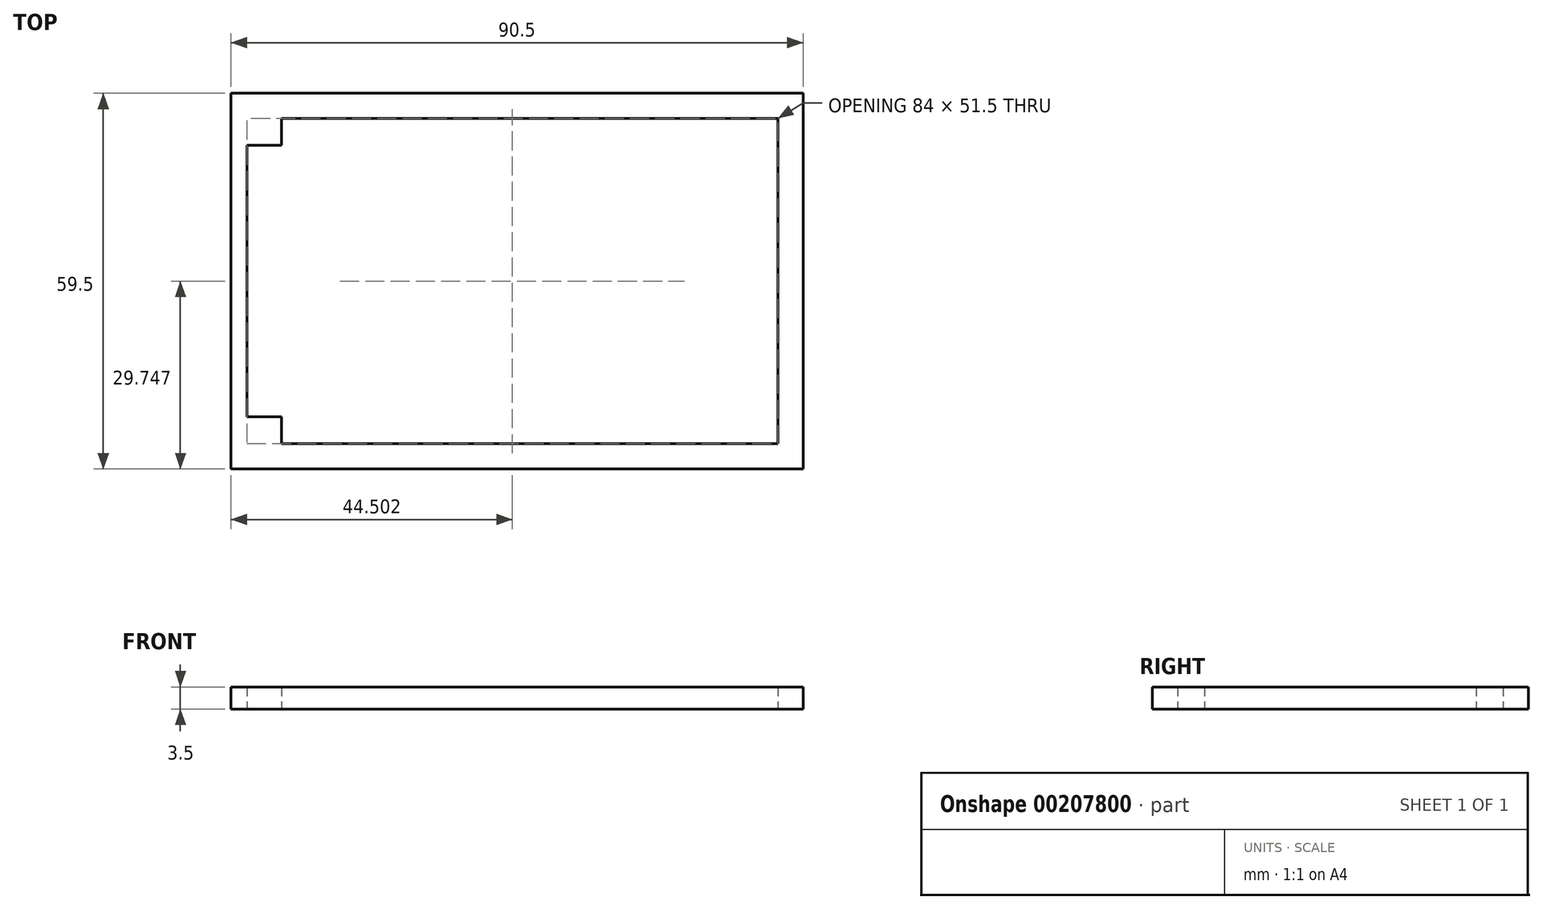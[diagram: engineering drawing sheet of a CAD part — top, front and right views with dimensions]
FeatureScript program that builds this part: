
annotation { "Feature Type Name" : "Feature", "Feature Type Description" : "" }
export const myFeature = defineFeature(function(context is Context, id is Id, definition is map)
    precondition{}
    {
        {
            var Q0;
            Q0=qCreatedBy(makeId("Top.planeOp"),FACE);
            var sketch = newSketch(context, id + "F0", { "sketchPlane" : qUnion([Q0])});
            skPoint(sketch, "E0.middle", {"position": v(0, 0) * mm});
            skLineSegment(sketch, "E1", {"start": v(-44.37, -47.66) * mm, "end": v(46.13, -47.66) * mm});
            skLineSegment(sketch, "E2", {"start": v(46.13, -47.66) * mm, "end": v(46.13, 11.84) * mm});
            skLineSegment(sketch, "E3", {"start": v(46.13, 11.84) * mm, "end": v(-44.37, 11.84) * mm});
            skLineSegment(sketch, "E4", {"start": v(-44.37, 11.84) * mm, "end": v(-44.37, -47.66) * mm});
            skLineSegment(sketch, "E5", {"start": v(-41.87, 3.59) * mm, "end": v(-36.37, 3.59) * mm});
            skLineSegment(sketch, "E6", {"start": v(-36.37, 3.59) * mm, "end": v(-36.37, 7.84) * mm});
            skLineSegment(sketch, "E7", {"start": v(-36.37, 7.84) * mm, "end": v(42.13, 7.84) * mm});
            skLineSegment(sketch, "E8", {"start": v(42.13, 7.84) * mm, "end": v(42.13, -43.66) * mm});
            skLineSegment(sketch, "E9", {"start": v(42.13, -43.66) * mm, "end": v(-36.37, -43.66) * mm});
            skLineSegment(sketch, "E10", {"start": v(-36.37, -43.66) * mm, "end": v(-36.37, -39.41) * mm});
            skLineSegment(sketch, "E11", {"start": v(-36.37, -39.41) * mm, "end": v(-41.87, -39.41) * mm});
            skLineSegment(sketch, "E12", {"start": v(-41.87, -39.41) * mm, "end": v(-41.87, 3.59) * mm});
            skSolve(sketch);
        }
        {
            var Q0;
            Q0 = qSketchRegion(id + "F0", true);
            extrude(context, id + "F1", {"entities" : qUnion([Q0]), "depth" : 3.5 * mm});
        }
    });
